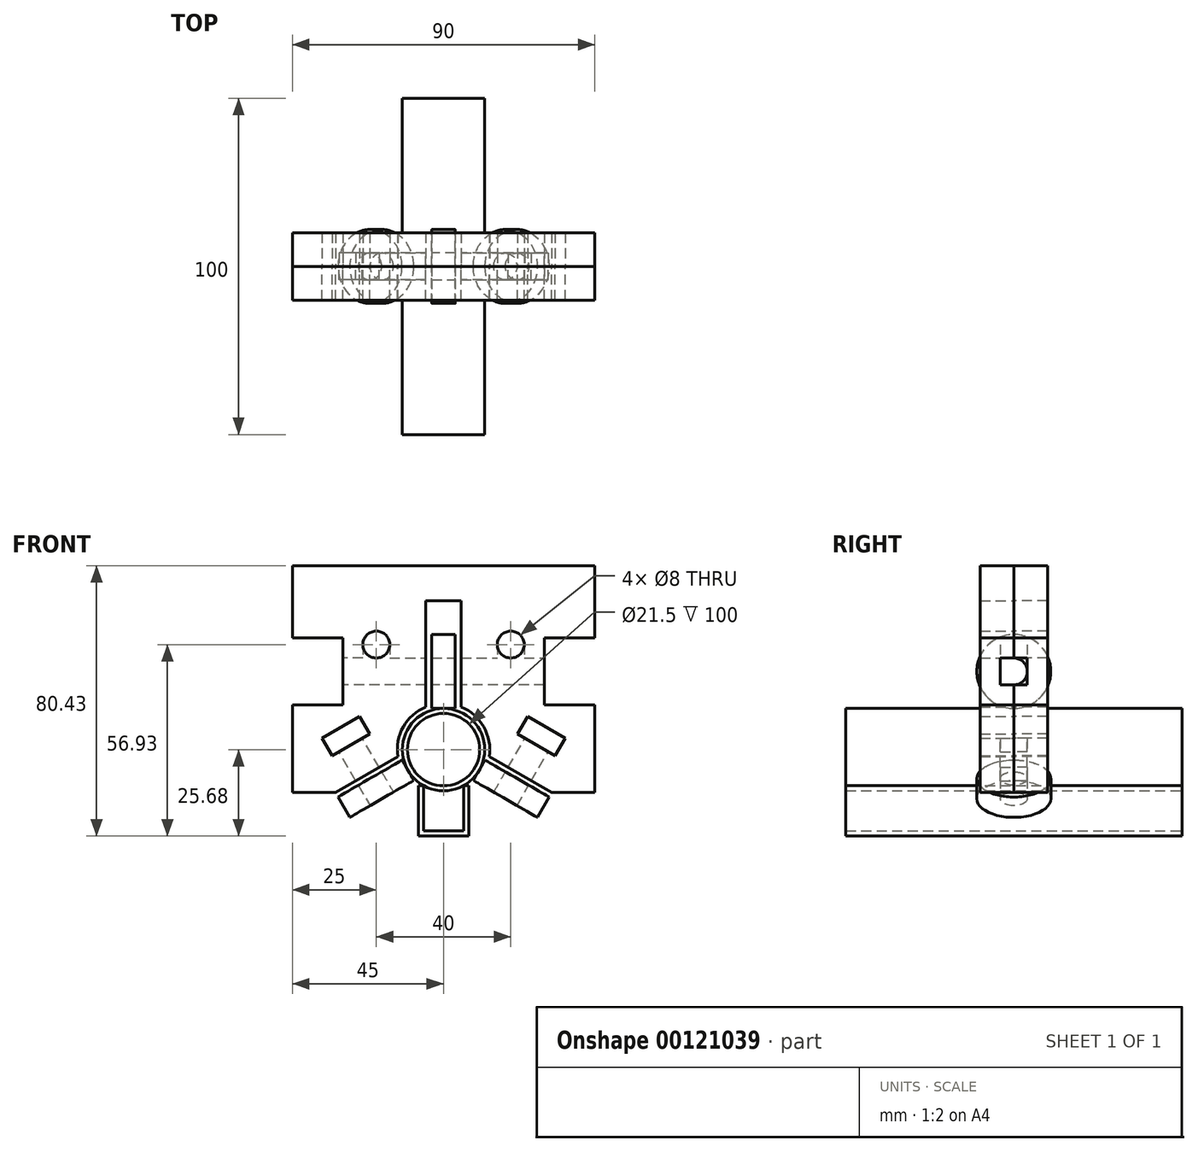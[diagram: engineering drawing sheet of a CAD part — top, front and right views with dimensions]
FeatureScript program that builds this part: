
annotation { "Feature Type Name" : "Feature", "Feature Type Description" : "" }
export const myFeature = defineFeature(function(context is Context, id is Id, definition is map)
    precondition{}
    {
        {
            var Q0;
            Q0=qCreatedBy(makeId("Front.planeOp"),FACE);
            var sketch = newSketch(context, id + "F0", { "sketchPlane" : qUnion([Q0])});
            skCircle(sketch, "E0", {"center": v(0, 0) * mm, "radius": 12.25 * mm});
            skCircle(sketch, "E1", {"center": v(0, 0) * mm, "radius": 10.75 * mm});
            skLineSegment(sketch, "E2", {"start": v(0, -24.18) * mm, "end": v(-6, -24.18) * mm});
            skLineSegment(sketch, "E3", {"start": v(-6, -24.18) * mm, "end": v(-6, -10.68) * mm});
            skLineSegment(sketch, "E4", {"start": v(-6, -10.68) * mm, "end": v(-7.5, -10.68) * mm});
            skLineSegment(sketch, "E5", {"start": v(-7.5, -10.68) * mm, "end": v(-7.5, -25.68) * mm});
            skLineSegment(sketch, "E6", {"start": v(-7.5, -25.68) * mm, "end": v(0, -25.68) * mm});
            skLineSegment(sketch, "E7.MirrorCS", {"start": v(6, -10.68) * mm, "end": v(7.5, -10.68) * mm});
            skLineSegment(sketch, "E8.MirrorCS", {"start": v(6, -24.18) * mm, "end": v(6, -10.68) * mm});
            skLineSegment(sketch, "E9.MirrorCS", {"start": v(0, -24.18) * mm, "end": v(6, -24.18) * mm});
            skLineSegment(sketch, "E10.MirrorCS", {"start": v(7.5, -25.68) * mm, "end": v(0, -25.68) * mm});
            skLineSegment(sketch, "E11.MirrorCS", {"start": v(7.5, -10.68) * mm, "end": v(7.5, -25.68) * mm});
            skSolve(sketch);
        }
        {
            var Q0;
            Q0=makeQuery(id+"F0.imprint","IMPRINT",FACE,{"disambiguationData":[TD([[makeQuery(id+"F0.imprint","IMPRINT",EDGE,{"derivedFrom":sQuery(id+"F0.wireOp",EDGE,"E2")}),1.0]])]});
            var Q1;
            Q1=makeQuery(id+"F0.imprint","IMPRINT",FACE,{"disambiguationData":[TD([[makeQuery(id+"F0.imprint","IMPRINT",EDGE,{"derivedFrom":sQuery(id+"F0.wireOp",EDGE,"E1")}),-1.0]])]});
            extrude(context, id + "F1", {"entities" : qUnion([Q0, Q1]), "endBound" : BoundingType.SYMMETRIC, "depth" : 100 * mm});
        }
        {
            var Q0;
            Q0=qCreatedBy(makeId("Right.planeOp"),FACE);
            var sketch = newSketch(context, id + "F2", { "sketchPlane" : qUnion([Q0])});
            skCircle(sketch, "E12", {"center": v(0, 23.25) * mm, "radius": 11 * mm});
            skCircle(sketch, "E13", {"center": v(0, 23.25) * mm, "radius": 4 * mm});
            skLineSegment(sketch, "E14", {"start": v(-50, 12.25) * mm, "end": v(50, 12.25) * mm, "construction": true});
            skSolve(sketch);
        }
        {
            var Q0;
            Q0=qSketchRegion(id+"F2",true);
            extrude(context, id + "F3", {"entities" : qUnion([Q0]), "endBound" : BoundingType.SYMMETRIC, "depth" : 7 * mm});
        }
        {
            var Q0;
            Q0=qCreatedBy(makeId("Top.planeOp"),FACE);
            var sketch = newSketch(context, id + "F4", { "sketchPlane" : qUnion([Q0])});
            skLineSegment(sketch, "E15.0", {"start": v(12.25, 50) * mm, "end": v(-12.25, 50) * mm, "construction": true});
            skLineSegment(sketch, "E16.0", {"start": v(12.25, -50) * mm, "end": v(-12.25, -50) * mm, "construction": true});
            skLineSegment(sketch, "E17", {"start": v(0, 50) * mm, "end": v(0, -50) * mm, "construction": true});
            skSolve(sketch);
        }
        {
            var Q0;
            Q0=makeQuery(id+"F3.opExtrude","SWEPT_BODY",BODY,{"disambiguationData":[OSD([sQuery(id+"F2.wireOp",EDGE,"E12"),sQuery(id+"F2.wireOp",EDGE,"E13")])]});
            var Q1;
            Q1=sQuery(id+"F4.wireOp",EDGE,"E17");
            circularPattern(context, id + "F5", {"entities" : qUnion([Q0]), "axis" : qUnion([Q1]), "angle" : 120 * degree, "instanceCount" : 3});
        }
        {
            var Q0;
            Q0=qCreatedBy(makeId("Front.planeOp"),FACE);
            var sketch = newSketch(context, id + "F6", { "sketchPlane" : qUnion([Q0])});
            skLineSegment(sketch, "E18", {"start": v(31.41, -14.1) * mm, "end": v(27.91, -20.16) * mm, "construction": true});
            skLineSegment(sketch, "E19", {"start": v(8.86, -9.16) * mm, "end": v(12.36, -3.1) * mm, "construction": true});
            skLineSegment(sketch, "E20.0", {"start": v(31.41, -14.1) * mm, "end": v(12.36, -3.1) * mm, "construction": true});
            skLineSegment(sketch, "E21", {"start": v(13.6, -2.07) * mm, "end": v(32.16, -12.8) * mm});
            skLineSegment(sketch, "E22", {"start": v(22, 4.62) * mm, "end": v(33.18, -1.83) * mm});
            skPoint(sketch, "E23", {"position": v(22.88, -7.43) * mm});
            skLineSegment(sketch, "E24.0", {"start": v(25.35, -10.6) * mm, "end": v(18.42, -6.6) * mm, "construction": true});
            skLineSegment(sketch, "E25", {"start": v(18.42, -6.6) * mm, "end": v(24.17, 3.37) * mm, "construction": true});
            skLineSegment(sketch, "E26", {"start": v(25.35, -10.6) * mm, "end": v(31.1, -0.63) * mm, "construction": true});
            skLineSegment(sketch, "E27", {"start": v(22, 4.62) * mm, "end": v(25, 9.81) * mm});
            skLineSegment(sketch, "E28", {"start": v(25, 9.81) * mm, "end": v(36.18, 3.36) * mm});
            skLineSegment(sketch, "E29", {"start": v(33.18, -1.83) * mm, "end": v(36.18, 3.36) * mm});
            skLineSegment(sketch, "E30", {"start": v(12.6, -13.04) * mm, "end": v(23.88, -19.56) * mm, "construction": true});
            skLineSegment(sketch, "E31", {"start": v(-3.5, 27.25) * mm, "end": v(45, 27.25) * mm, "construction": true});
            skLineSegment(sketch, "E32", {"start": v(45, 19.25) * mm, "end": v(-3.5, 19.25) * mm, "construction": true});
            skArc(sketch, "E33", {"start": v(13.6, -2.07) * mm, "mid": v(11.97, 6.76) * mm, "end": v(5.25, 12.7) * mm});
            skLineSegment(sketch, "E34", {"start": v(5.25, 12.7) * mm, "end": v(5.25, 44.25) * mm});
            skLineSegment(sketch, "E35", {"start": v(5.25, 44.25) * mm, "end": v(0, 44.25) * mm});
            skLineSegment(sketch, "E36", {"start": v(-3.5, 34.25) * mm, "end": v(3.5, 34.25) * mm, "construction": true});
            skLineSegment(sketch, "E37", {"start": v(0, 54.75) * mm, "end": v(45, 54.75) * mm});
            skLineSegment(sketch, "E38", {"start": v(32.16, -12.8) * mm, "end": v(45, -12.8) * mm});
            skLineSegment(sketch, "E39", {"start": v(45, -12.8) * mm, "end": v(45, 13.25) * mm});
            skLineSegment(sketch, "E40.MirrorCS", {"start": v(-5.25, 44.25) * mm, "end": v(0, 44.25) * mm});
            skLineSegment(sketch, "E41.MirrorCS", {"start": v(-5.25, 12.7) * mm, "end": v(-5.25, 44.25) * mm});
            skArc(sketch, "E42.MirrorCS", {"start": v(-13.6, -2.07) * mm, "mid": v(-11.97, 6.76) * mm, "end": v(-5.25, 12.7) * mm});
            skLineSegment(sketch, "E43.MirrorCS", {"start": v(-13.6, -2.07) * mm, "end": v(-32.16, -12.8) * mm});
            skLineSegment(sketch, "E44.MirrorCS", {"start": v(-32.16, -12.8) * mm, "end": v(-45, -12.8) * mm});
            skLineSegment(sketch, "E45.MirrorCS", {"start": v(-45, -12.8) * mm, "end": v(-45, 13.25) * mm});
            skLineSegment(sketch, "E46.MirrorCS", {"start": v(0, 54.75) * mm, "end": v(-45, 54.75) * mm});
            skLineSegment(sketch, "E47.MirrorCS", {"start": v(-25, 9.81) * mm, "end": v(-36.18, 3.36) * mm});
            skLineSegment(sketch, "E48.MirrorCS", {"start": v(-33.18, -1.83) * mm, "end": v(-36.18, 3.36) * mm});
            skLineSegment(sketch, "E49.MirrorCS", {"start": v(-22, 4.62) * mm, "end": v(-33.18, -1.83) * mm});
            skLineSegment(sketch, "E50.MirrorCS", {"start": v(-22, 4.62) * mm, "end": v(-25, 9.81) * mm});
            skLineSegment(sketch, "E51.MirrorCS", {"start": v(-18.42, -6.6) * mm, "end": v(-24.17, 3.37) * mm, "construction": true});
            skLineSegment(sketch, "E52.MirrorCS", {"start": v(-25.35, -10.6) * mm, "end": v(-31.1, -0.63) * mm, "construction": true});
            skLineSegment(sketch, "E53.MirrorCS", {"start": v(3.5, 27.25) * mm, "end": v(-45, 27.25) * mm, "construction": true});
            skLineSegment(sketch, "E54.MirrorCS", {"start": v(-45, 19.25) * mm, "end": v(3.5, 19.25) * mm, "construction": true});
            skCircle(sketch, "E55", {"center": v(-20, 31.25) * mm, "radius": 4 * mm});
            skLineSegment(sketch, "E56", {"start": v(-45, 35.25) * mm, "end": v(45, 35.25) * mm, "construction": true});
            skCircle(sketch, "E57.MirrorC", {"center": v(20, 31.25) * mm, "radius": 4 * mm});
            skLineSegment(sketch, "E58", {"start": v(30, 33.25) * mm, "end": v(30, 13.25) * mm});
            skLineSegment(sketch, "E59", {"start": v(30, 13.25) * mm, "end": v(45, 13.25) * mm});
            skLineSegment(sketch, "E60", {"start": v(30, 33.25) * mm, "end": v(45, 33.25) * mm});
            skLineSegment(sketch, "E61", {"start": v(-45, 23.25) * mm, "end": v(45, 23.25) * mm, "construction": true});
            skLineSegment(sketch, "E62", {"start": v(-45, 33.25) * mm, "end": v(-30, 33.25) * mm});
            skLineSegment(sketch, "E63", {"start": v(-30, 33.25) * mm, "end": v(-30, 13.25) * mm});
            skLineSegment(sketch, "E64", {"start": v(-30, 13.25) * mm, "end": v(-45, 13.25) * mm});
            skLineSegment(sketch, "E65.trimOffspring", {"start": v(-45, 33.25) * mm, "end": v(-45, 54.75) * mm});
            skLineSegment(sketch, "E66.trimOffspring", {"start": v(45, 33.25) * mm, "end": v(45, 54.75) * mm});
            skSolve(sketch);
        }
        {
            var Q0;
            Q0 = qSketchRegion(id + "F6", true);
            extrude(context, id + "F7", {"entities" : qUnion([Q0]), "depth" : 10 * mm});
        }
        {
            var Q0;
            Q0=makeQuery(id+"F6.imprint","IMPRINT",FACE,{"disambiguationData":[TD([[makeQuery(id+"F6.imprint","IMPRINT",EDGE,{"derivedFrom":sQuery(id+"F6.wireOp",EDGE,"E21")}),1.0]])]});
            var sketch = newSketch(context, id + "F8", { "sketchPlane" : qUnion([Q0])});
            skLineSegment(sketch, "E67.0", {"start": v(-3.5, 27.25) * mm, "end": v(45, 27.25) * mm});
            skLineSegment(sketch, "E68.0", {"start": v(3.5, 27.25) * mm, "end": v(-45, 27.25) * mm});
            skLineSegment(sketch, "E69.0", {"start": v(-45, 19.25) * mm, "end": v(3.5, 19.25) * mm});
            skLineSegment(sketch, "E70.0", {"start": v(45, 19.25) * mm, "end": v(-3.5, 19.25) * mm});
            skLineSegment(sketch, "E71.0", {"start": v(18.42, -6.6) * mm, "end": v(24.17, 3.37) * mm});
            skLineSegment(sketch, "E72.0", {"start": v(25.35, -10.6) * mm, "end": v(31.1, -0.63) * mm});
            skLineSegment(sketch, "E73.0", {"start": v(13.6, -2.07) * mm, "end": v(32.16, -12.8) * mm});
            skLineSegment(sketch, "E74.0", {"start": v(22, 4.62) * mm, "end": v(33.18, -1.83) * mm});
            skLineSegment(sketch, "E75.0", {"start": v(45, -12.8) * mm, "end": v(45, 13.25) * mm});
            skLineSegment(sketch, "E76.0", {"start": v(-45, -12.8) * mm, "end": v(-45, 13.25) * mm});
            skLineSegment(sketch, "E77.0", {"start": v(-22, 4.62) * mm, "end": v(-33.18, -1.83) * mm});
            skLineSegment(sketch, "E78.0", {"start": v(-25.35, -10.6) * mm, "end": v(-31.1, -0.63) * mm});
            skLineSegment(sketch, "E79.0", {"start": v(-13.6, -2.07) * mm, "end": v(-32.16, -12.8) * mm});
            skLineSegment(sketch, "E80.0", {"start": v(-18.42, -6.6) * mm, "end": v(-24.17, 3.37) * mm});
            skCircle(sketch, "E81.0", {"center": v(-20, 31.25) * mm, "radius": 4 * mm});
            skCircle(sketch, "E82.0", {"center": v(20, 31.25) * mm, "radius": 4 * mm});
            skLineSegment(sketch, "E83", {"start": v(-24, 31.25) * mm, "end": v(-24, 27.25) * mm});
            skPoint(sketch, "E83.endSnap0", {"position": v(-20.75, 27.25) * mm});
            skLineSegment(sketch, "E84", {"start": v(-16, 31.25) * mm, "end": v(-16, 27.25) * mm});
            skLineSegment(sketch, "E85.MirrorCS", {"start": v(16, 31.25) * mm, "end": v(16, 27.25) * mm});
            skLineSegment(sketch, "E86.MirrorCS", {"start": v(24, 31.25) * mm, "end": v(24, 27.25) * mm});
            skLineSegment(sketch, "E87", {"start": v(-45, 27.25) * mm, "end": v(-45, 19.25) * mm});
            skLineSegment(sketch, "E88", {"start": v(45, 27.25) * mm, "end": v(45, 19.25) * mm});
            skSolve(sketch);
        }
        {
            var Q0;
            Q0 = qSketchRegion(id + "F8", true);
            extrude(context, id + "F9", {"entities" : qUnion([Q0]), "operationType" : NewBodyOperationType.REMOVE, "depth" : 4 * mm});
        }
        {
            var Q0;
            Q0=makeQuery(id+"F7.opExtrude","SWEPT_BODY",BODY,{"disambiguationData":[OSD([sQuery(id+"F6.wireOp",EDGE,"E21"),sQuery(id+"F6.wireOp",EDGE,"E22"),sQuery(id+"F6.wireOp",EDGE,"E27"),sQuery(id+"F6.wireOp",EDGE,"E28"),sQuery(id+"F6.wireOp",EDGE,"E29"),sQuery(id+"F6.wireOp",EDGE,"E33"),sQuery(id+"F6.wireOp",EDGE,"E34"),sQuery(id+"F6.wireOp",EDGE,"E35"),sQuery(id+"F6.wireOp",EDGE,"E37"),sQuery(id+"F6.wireOp",EDGE,"E38"),sQuery(id+"F6.wireOp",EDGE,"E39"),sQuery(id+"F6.wireOp",EDGE,"E40.MirrorCS"),sQuery(id+"F6.wireOp",EDGE,"E41.MirrorCS"),sQuery(id+"F6.wireOp",EDGE,"E42.MirrorCS"),sQuery(id+"F6.wireOp",EDGE,"E43.MirrorCS"),sQuery(id+"F6.wireOp",EDGE,"E44.MirrorCS"),sQuery(id+"F6.wireOp",EDGE,"E45.MirrorCS"),sQuery(id+"F6.wireOp",EDGE,"E46.MirrorCS"),sQuery(id+"F6.wireOp",EDGE,"E47.MirrorCS"),sQuery(id+"F6.wireOp",EDGE,"E48.MirrorCS"),sQuery(id+"F6.wireOp",EDGE,"E49.MirrorCS"),sQuery(id+"F6.wireOp",EDGE,"E50.MirrorCS"),sQuery(id+"F6.wireOp",EDGE,"E55"),sQuery(id+"F6.wireOp",EDGE,"E57.MirrorC")])]});
            var Q1;
            {var subQ1=sQuery(id+"F6.wireOp",EDGE,"E57.MirrorC");var subQ2=sQuery(id+"F6.wireOp",EDGE,"E46.MirrorCS");var subQ3=sQuery(id+"F6.wireOp",EDGE,"E37");var subQ4=sQuery(id+"F6.wireOp",EDGE,"E41.MirrorCS");var subQ5=sQuery(id+"F6.wireOp",EDGE,"E34");var subQ6=sQuery(id+"F6.wireOp",EDGE,"E45.MirrorCS");var subQ7=sQuery(id+"F6.wireOp",EDGE,"E40.MirrorCS");var subQ8=sQuery(id+"F6.wireOp",EDGE,"E35");var subQ10=sQuery(id+"F6.wireOp",EDGE,"E55");var subQ11=sQuery(id+"F6.wireOp",EDGE,"E39");Q1=makeQuery(id+"F9.boolean.opBoolean","SPLIT",FACE,{"disambiguationData":[TD([makeQuery(id+"F7.opExtrude","SWEPT_FACE",FACE,{"disambiguationData":[OSD([subQ10])]})])],"derivedFrom":makeQuery(id+"F7.opExtrude","CAP_FACE",FACE,{"disambiguationData":[OSD([sQuery(id+"F6.wireOp",EDGE,"E21"),sQuery(id+"F6.wireOp",EDGE,"E22"),sQuery(id+"F6.wireOp",EDGE,"E27"),sQuery(id+"F6.wireOp",EDGE,"E28"),sQuery(id+"F6.wireOp",EDGE,"E29"),sQuery(id+"F6.wireOp",EDGE,"E33"),subQ5,subQ8,subQ3,sQuery(id+"F6.wireOp",EDGE,"E38"),subQ11,subQ7,subQ4,sQuery(id+"F6.wireOp",EDGE,"E42.MirrorCS"),sQuery(id+"F6.wireOp",EDGE,"E43.MirrorCS"),sQuery(id+"F6.wireOp",EDGE,"E44.MirrorCS"),subQ6,subQ2,sQuery(id+"F6.wireOp",EDGE,"E47.MirrorCS"),sQuery(id+"F6.wireOp",EDGE,"E48.MirrorCS"),sQuery(id+"F6.wireOp",EDGE,"E49.MirrorCS"),sQuery(id+"F6.wireOp",EDGE,"E50.MirrorCS"),subQ10,subQ1])],"isStart":true})});}
            mirror(context, id + "F10", {"entities" : qUnion([Q0]), "mirrorPlane" : qUnion([Q1])});
        }
    });
